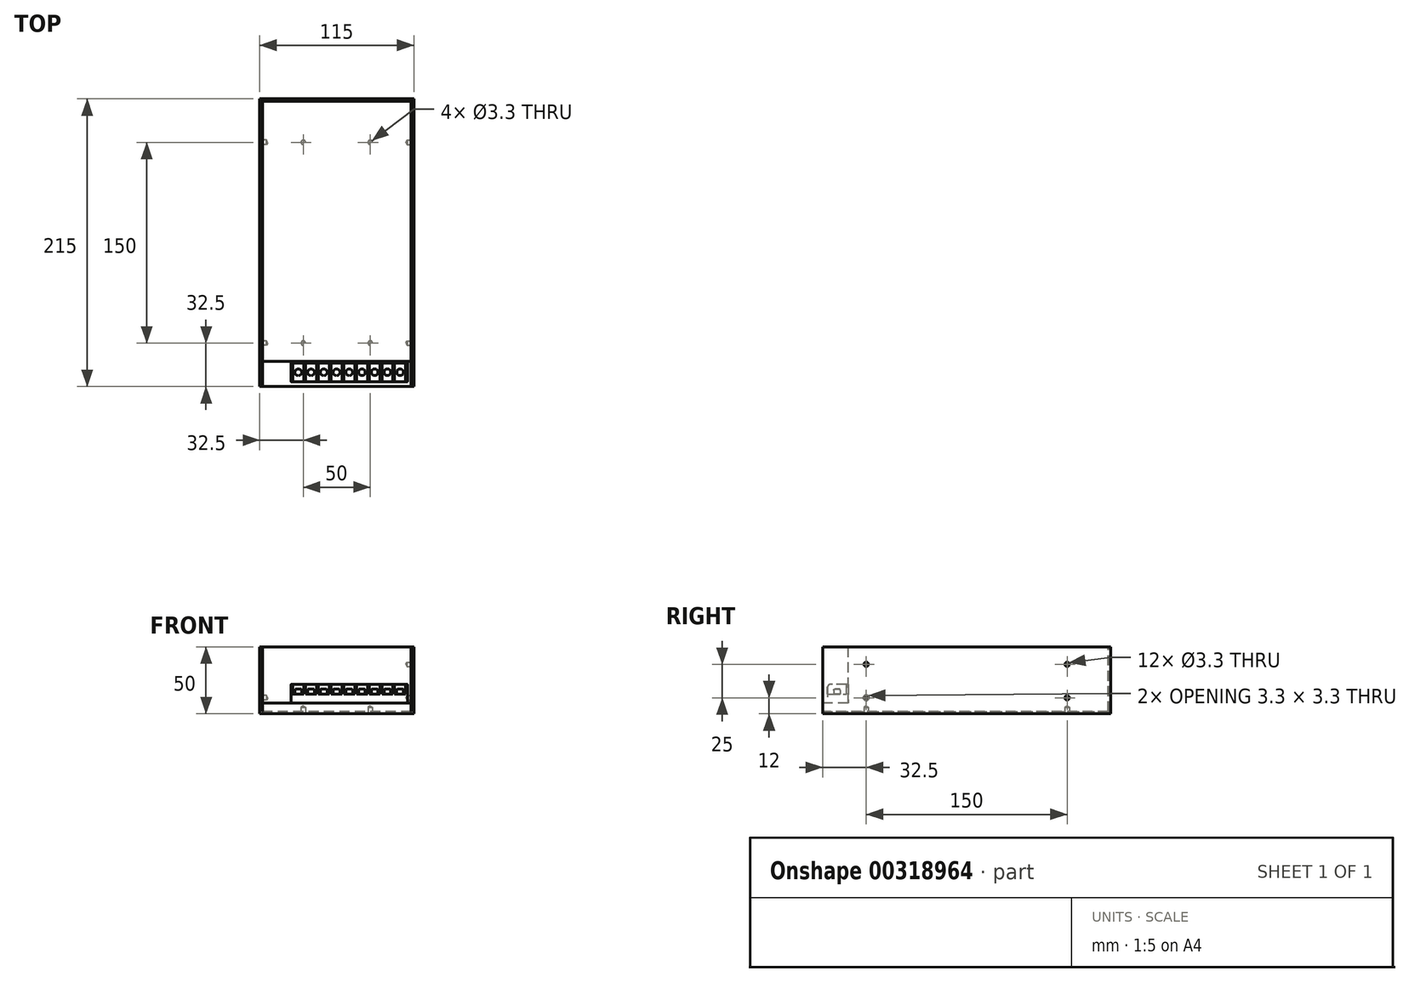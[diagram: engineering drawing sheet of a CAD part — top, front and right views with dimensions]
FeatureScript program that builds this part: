
annotation { "Feature Type Name" : "Feature", "Feature Type Description" : "" }
export const myFeature = defineFeature(function(context is Context, id is Id, definition is map)
    precondition{}
    {
        {
            var Q0;
            Q0=qCreatedBy(makeId("Front.planeOp"),FACE);
            var sketch = newSketch(context, id + "F0", { "sketchPlane" : qUnion([Q0])});
            skLineSegment(sketch, "E0.bottom", {"start": v(-57.5, 25) * mm, "end": v(0, 25) * mm});
            skLineSegment(sketch, "E0.top", {"start": v(-57.5, -25) * mm, "end": v(0, -25) * mm});
            skLineSegment(sketch, "E0.left", {"start": v(-57.5, 25) * mm, "end": v(-57.5, -25) * mm});
            skLineSegment(sketch, "E0.right", {"start": v(0, 25) * mm, "end": v(0, -25) * mm});
            skLineSegment(sketch, "E1", {"start": v(0, 0) * mm, "end": v(0, 48.13) * mm, "construction": true});
            skLineSegment(sketch, "E2", {"start": v(0, 0) * mm, "end": v(-98.9, 0) * mm, "construction": true});
            skPoint(sketch, "E2.endSnap0", {"position": v(0, 0) * mm});
            skSolve(sketch);
        }
        {
            var Q0;
            Q0=makeQuery(id+"F0.imprint","IMPRINT",FACE,{"disambiguationData":[TD([[makeQuery(id+"F0.imprint","IMPRINT",EDGE,{"derivedFrom":sQuery(id+"F0.wireOp",EDGE,"E0.bottom")}),-1.0]])]});
            extrude(context, id + "F1", {"entities" : qUnion([Q0]), "endBound" : BoundingType.SYMMETRIC, "depth" : 215 * mm});
        }
        {
            var Q0;
            Q0=makeQuery(id+"F1.opExtrude","SWEPT_FACE",FACE,{"disambiguationData":[OSD([sQuery(id+"F0.wireOp",EDGE,"E0.bottom")])]});
            var sketch = newSketch(context, id + "F2", { "sketchPlane" : qUnion([Q0])});
            skLineSegment(sketch, "E3.bottom", {"start": v(0, -107.5) * mm, "end": v(-55.8, -107.5) * mm});
            skLineSegment(sketch, "E3.top", {"start": v(0, -88.5) * mm, "end": v(-55.8, -88.5) * mm});
            skLineSegment(sketch, "E3.left", {"start": v(0, -107.5) * mm, "end": v(0, -88.5) * mm});
            skLineSegment(sketch, "E3.right", {"start": v(-55.8, -107.5) * mm, "end": v(-55.8, -88.5) * mm});
            skSolve(sketch);
        }
        {
            var Q0;
            Q0=makeQuery(id+"F2.imprint","IMPRINT",FACE,{"disambiguationData":[TD([[makeQuery(id+"F2.imprint","IMPRINT",EDGE,{"derivedFrom":sQuery(id+"F2.wireOp",EDGE,"E3.bottom")}),1.0]])]});
            extrude(context, id + "F3", {"entities" : qUnion([Q0]), "operationType" : NewBodyOperationType.REMOVE, "oppositeDirection" : true, "depth" : 42 * mm});
        }
        {
            var Q0;
            Q0=makeQuery(id+"F1.opExtrude","SWEPT_FACE",FACE,{"disambiguationData":[OSD([sQuery(id+"F0.wireOp",EDGE,"E0.bottom")])]});
            var sketch = newSketch(context, id + "F4", { "sketchPlane" : qUnion([Q0])});
            skLineSegment(sketch, "E4", {"start": v(-55.8, -107.5) * mm, "end": v(-55.8, 107.5) * mm});
            skLineSegment(sketch, "E5", {"start": v(-55.8, 107.5) * mm, "end": v(-55.5, 107.5) * mm});
            skLineSegment(sketch, "E6", {"start": v(-55.5, 107.5) * mm, "end": v(-55.5, 105.8) * mm});
            skLineSegment(sketch, "E7", {"start": v(-55.5, 105.8) * mm, "end": v(0, 105.8) * mm});
            skLineSegment(sketch, "E8", {"start": v(0, 105.8) * mm, "end": v(0, 105.5) * mm});
            skLineSegment(sketch, "E9", {"start": v(0, 105.5) * mm, "end": v(-55.5, 105.5) * mm});
            skLineSegment(sketch, "E10", {"start": v(-55.5, 105.5) * mm, "end": v(-55.5, -107.5) * mm});
            skLineSegment(sketch, "E11", {"start": v(-55.5, -107.5) * mm, "end": v(-55.8, -107.5) * mm});
            skSolve(sketch);
        }
        {
            var Q0;
            {var subQ1=sQuery(id+"F4.wireOp",EDGE,"E5");Q0=makeQuery(id+"F4.imprint","IMPRINT",FACE,{"disambiguationData":[TD([[makeQuery(id+"F4.imprint","IMPRINT",EDGE,{"derivedFrom":subQ1}),-1.0]])]});}
            var Q1;
            {var subQ0=sQuery(id+"F4.wireOp",EDGE,"E11");Q1=makeQuery(id+"F4.imprint","IMPRINT",FACE,{"disambiguationData":[TD([[makeQuery(id+"F4.imprint","IMPRINT",EDGE,{"derivedFrom":subQ0}),-1.0]])]});}
            extrude(context, id + "F5", {"entities" : qUnion([Q0, Q1]), "operationType" : NewBodyOperationType.REMOVE, "oppositeDirection" : true, "depth" : 48.3 * mm});
        }
        {
            var Q0;
            Q0=makeQuery(id+"F1.opExtrude","SWEPT_BODY",BODY,{"disambiguationData":[OSD([sQuery(id+"F0.wireOp",EDGE,"E0.bottom"),sQuery(id+"F0.wireOp",EDGE,"E0.top"),sQuery(id+"F0.wireOp",EDGE,"E0.left"),sQuery(id+"F0.wireOp",EDGE,"E0.right")])]});
            var Q1;
            Q1=qCreatedBy(makeId("Right.planeOp"),FACE);
            mirror(context, id + "F6", {"operationType" : NewBodyOperationType.ADD, "entities" : qUnion([Q0]), "mirrorPlane" : qUnion([Q1])});
        }
        {
            var Q0;
            {var subQ0=makeQuery(id+"F3.boolean.opBoolean","COPY",FACE,{"derivedFrom":makeQuery(id+"F3.opExtrude","CAP_FACE",FACE,{"disambiguationData":[OSD([sQuery(id+"F2.wireOp",EDGE,"E3.bottom"),sQuery(id+"F2.wireOp",EDGE,"E3.top"),sQuery(id+"F2.wireOp",EDGE,"E3.left"),sQuery(id+"F2.wireOp",EDGE,"E3.right")])],"isStart":false})});Q0=makeQuery(id+"F6.boolean.opBoolean","MERGE",FACE,{"derivedFrom":[subQ0,makeQuery(id+"F6.opPattern","COPY",FACE,{"derivedFrom":subQ0,"instanceName":"1"})]});}
            var sketch = newSketch(context, id + "F7", { "sketchPlane" : qUnion([Q0])});
            skLineSegment(sketch, "E12.bottom", {"start": v(-34.2, -88.5) * mm, "end": v(52.8, -88.5) * mm});
            skLineSegment(sketch, "E12.top", {"start": v(-34.2, -103.8) * mm, "end": v(52.8, -103.8) * mm});
            skLineSegment(sketch, "E12.left", {"start": v(-34.2, -88.5) * mm, "end": v(-34.2, -103.8) * mm});
            skLineSegment(sketch, "E12.right", {"start": v(52.8, -88.5) * mm, "end": v(52.8, -103.8) * mm});
            skSolve(sketch);
        }
        {
            var Q0;
            Q0=makeQuery(id+"F7.imprint","IMPRINT",FACE,{"disambiguationData":[TD([[makeQuery(id+"F7.imprint","IMPRINT",EDGE,{"derivedFrom":sQuery(id+"F7.wireOp",EDGE,"E12.bottom")}),1.0]])]});
            extrude(context, id + "F8", {"entities" : qUnion([Q0]), "depth" : 14 * mm});
        }
        {
            var Q0;
            Q0=makeQuery(id+"F8.opExtrude","CAP_FACE",FACE,{"disambiguationData":[OSD([sQuery(id+"F7.wireOp",EDGE,"E12.bottom"),sQuery(id+"F7.wireOp",EDGE,"E12.top"),sQuery(id+"F7.wireOp",EDGE,"E12.left"),sQuery(id+"F7.wireOp",EDGE,"E12.right")])],"isStart":false});
            var sketch = newSketch(context, id + "F9", { "sketchPlane" : qUnion([Q0])});
            skLineSegment(sketch, "E13", {"start": v(-32.8, -103.8) * mm, "end": v(-32.8, -89.8) * mm});
            skLineSegment(sketch, "E14", {"start": v(-32.8, -89.8) * mm, "end": v(-24.6, -89.8) * mm});
            skLineSegment(sketch, "E15", {"start": v(-24.6, -89.8) * mm, "end": v(-24.6, -103.8) * mm});
            skLineSegment(sketch, "E16", {"start": v(-24.6, -103.8) * mm, "end": v(-32.8, -103.8) * mm});
            skLineSegment(sketch, "E17.1.0.0", {"start": v(-23.3, -103.8) * mm, "end": v(-23.3, -89.8) * mm});
            skLineSegment(sketch, "E17.1.0.1", {"start": v(-15.1, -103.8) * mm, "end": v(-23.3, -103.8) * mm});
            skLineSegment(sketch, "E17.1.0.2", {"start": v(-15.1, -89.8) * mm, "end": v(-15.1, -103.8) * mm});
            skLineSegment(sketch, "E17.1.0.3", {"start": v(-23.3, -89.8) * mm, "end": v(-15.1, -89.8) * mm});
            skLineSegment(sketch, "E17.2.0.0", {"start": v(-13.8, -103.8) * mm, "end": v(-13.8, -89.8) * mm});
            skLineSegment(sketch, "E17.2.0.1", {"start": v(-5.6, -103.8) * mm, "end": v(-13.8, -103.8) * mm});
            skLineSegment(sketch, "E17.2.0.2", {"start": v(-5.6, -89.8) * mm, "end": v(-5.6, -103.8) * mm});
            skLineSegment(sketch, "E17.2.0.3", {"start": v(-13.8, -89.8) * mm, "end": v(-5.6, -89.8) * mm});
            skLineSegment(sketch, "E17.3.0.0", {"start": v(-4.3, -103.8) * mm, "end": v(-4.3, -89.8) * mm});
            skLineSegment(sketch, "E17.3.0.1", {"start": v(3.9, -103.8) * mm, "end": v(-4.3, -103.8) * mm});
            skLineSegment(sketch, "E17.3.0.2", {"start": v(3.9, -89.8) * mm, "end": v(3.9, -103.8) * mm});
            skLineSegment(sketch, "E17.3.0.3", {"start": v(-4.3, -89.8) * mm, "end": v(3.9, -89.8) * mm});
            skLineSegment(sketch, "E17.4.0.0", {"start": v(5.2, -103.8) * mm, "end": v(5.2, -89.8) * mm});
            skLineSegment(sketch, "E17.4.0.1", {"start": v(13.4, -103.8) * mm, "end": v(5.2, -103.8) * mm});
            skLineSegment(sketch, "E17.4.0.2", {"start": v(13.4, -89.8) * mm, "end": v(13.4, -103.8) * mm});
            skLineSegment(sketch, "E17.4.0.3", {"start": v(5.2, -89.8) * mm, "end": v(13.4, -89.8) * mm});
            skLineSegment(sketch, "E17.5.0.0", {"start": v(14.7, -103.8) * mm, "end": v(14.7, -89.8) * mm});
            skLineSegment(sketch, "E17.5.0.1", {"start": v(22.9, -103.8) * mm, "end": v(14.7, -103.8) * mm});
            skLineSegment(sketch, "E17.5.0.2", {"start": v(22.9, -89.8) * mm, "end": v(22.9, -103.8) * mm});
            skLineSegment(sketch, "E17.5.0.3", {"start": v(14.7, -89.8) * mm, "end": v(22.9, -89.8) * mm});
            skLineSegment(sketch, "E17.6.0.0", {"start": v(24.2, -103.8) * mm, "end": v(24.2, -89.8) * mm});
            skLineSegment(sketch, "E17.6.0.1", {"start": v(32.4, -103.8) * mm, "end": v(24.2, -103.8) * mm});
            skLineSegment(sketch, "E17.6.0.2", {"start": v(32.4, -89.8) * mm, "end": v(32.4, -103.8) * mm});
            skLineSegment(sketch, "E17.6.0.3", {"start": v(24.2, -89.8) * mm, "end": v(32.4, -89.8) * mm});
            skLineSegment(sketch, "E17.7.0.0", {"start": v(33.7, -103.8) * mm, "end": v(33.7, -89.8) * mm});
            skLineSegment(sketch, "E17.7.0.1", {"start": v(41.9, -103.8) * mm, "end": v(33.7, -103.8) * mm});
            skLineSegment(sketch, "E17.7.0.2", {"start": v(41.9, -89.8) * mm, "end": v(41.9, -103.8) * mm});
            skLineSegment(sketch, "E17.7.0.3", {"start": v(33.7, -89.8) * mm, "end": v(41.9, -89.8) * mm});
            skLineSegment(sketch, "E17.8.0.0", {"start": v(43.2, -103.8) * mm, "end": v(43.2, -89.8) * mm});
            skLineSegment(sketch, "E17.8.0.1", {"start": v(51.4, -103.8) * mm, "end": v(43.2, -103.8) * mm});
            skLineSegment(sketch, "E17.8.0.2", {"start": v(51.4, -89.8) * mm, "end": v(51.4, -103.8) * mm});
            skLineSegment(sketch, "E17.8.0.3", {"start": v(43.2, -89.8) * mm, "end": v(51.4, -89.8) * mm});
            skLineSegment(sketch, "E17.direction1", {"start": v(-32.8, -103.8) * mm, "end": v(-23.3, -103.8) * mm, "construction": true});
            skSolve(sketch);
        }
        {
            var Q0;
            Q0=makeQuery(id+"F9.imprint","IMPRINT",FACE,{"disambiguationData":[TD([[makeQuery(id+"F9.imprint","IMPRINT",EDGE,{"derivedFrom":sQuery(id+"F9.wireOp",EDGE,"E13")}),-1.0]])]});
            var Q1;
            Q1=makeQuery(id+"F9.imprint","IMPRINT",FACE,{"disambiguationData":[TD([[makeQuery(id+"F9.imprint","IMPRINT",EDGE,{"derivedFrom":sQuery(id+"F9.wireOp",EDGE,"E17.1.0.0")}),-1.0]])]});
            var Q2;
            Q2=makeQuery(id+"F9.imprint","IMPRINT",FACE,{"disambiguationData":[TD([[makeQuery(id+"F9.imprint","IMPRINT",EDGE,{"derivedFrom":sQuery(id+"F9.wireOp",EDGE,"E17.2.0.0")}),-1.0]])]});
            var Q3;
            Q3=makeQuery(id+"F9.imprint","IMPRINT",FACE,{"disambiguationData":[TD([[makeQuery(id+"F9.imprint","IMPRINT",EDGE,{"derivedFrom":sQuery(id+"F9.wireOp",EDGE,"E17.3.0.0")}),-1.0]])]});
            var Q4;
            Q4=makeQuery(id+"F9.imprint","IMPRINT",FACE,{"disambiguationData":[TD([[makeQuery(id+"F9.imprint","IMPRINT",EDGE,{"derivedFrom":sQuery(id+"F9.wireOp",EDGE,"E17.4.0.0")}),-1.0]])]});
            var Q5;
            Q5=makeQuery(id+"F9.imprint","IMPRINT",FACE,{"disambiguationData":[TD([[makeQuery(id+"F9.imprint","IMPRINT",EDGE,{"derivedFrom":sQuery(id+"F9.wireOp",EDGE,"E17.5.0.0")}),-1.0]])]});
            var Q6;
            Q6=makeQuery(id+"F9.imprint","IMPRINT",FACE,{"disambiguationData":[TD([[makeQuery(id+"F9.imprint","IMPRINT",EDGE,{"derivedFrom":sQuery(id+"F9.wireOp",EDGE,"E17.6.0.0")}),-1.0]])]});
            var Q7;
            Q7=makeQuery(id+"F9.imprint","IMPRINT",FACE,{"disambiguationData":[TD([[makeQuery(id+"F9.imprint","IMPRINT",EDGE,{"derivedFrom":sQuery(id+"F9.wireOp",EDGE,"E17.7.0.0")}),-1.0]])]});
            var Q8;
            Q8=makeQuery(id+"F9.imprint","IMPRINT",FACE,{"disambiguationData":[TD([[makeQuery(id+"F9.imprint","IMPRINT",EDGE,{"derivedFrom":sQuery(id+"F9.wireOp",EDGE,"E17.8.0.0")}),-1.0]])]});
            extrude(context, id + "F10", {"entities" : qUnion([Q0, Q1, Q2, Q3, Q4, Q5, Q6, Q7, Q8]), "operationType" : NewBodyOperationType.REMOVE, "oppositeDirection" : true, "depth" : 7.4 * mm});
        }
        {
            var Q0;
            {var subQ0=sQuery(id+"F7.wireOp",EDGE,"E12.left");var subQ1=sQuery(id+"F7.wireOp",EDGE,"E12.top");Q0=makeQuery(id+"F10.boolean.opBoolean","SPLIT",EDGE,{"disambiguationData":[TD([makeQuery(id+"F8.opExtrude","SWEPT_FACE",FACE,{"disambiguationData":[OSD([subQ0])]})])],"derivedFrom":makeQuery(id+"F8.opExtrude","CAP_EDGE",EDGE,{"disambiguationData":[OSD([subQ1])],"isStart":false})});}
            var Q1;
            {var subQ0=sQuery(id+"F7.wireOp",EDGE,"E12.top");Q1=makeQuery(id+"F10.boolean.opBoolean","SPLIT",EDGE,{"disambiguationData":[TD([makeQuery(id+"F10.opExtrude","SWEPT_FACE",FACE,{"disambiguationData":[OSD([sQuery(id+"F9.wireOp",EDGE,"E15")])]})])],"derivedFrom":makeQuery(id+"F8.opExtrude","CAP_EDGE",EDGE,{"disambiguationData":[OSD([subQ0])],"isStart":false})});}
            var Q2;
            {var subQ0=sQuery(id+"F7.wireOp",EDGE,"E12.top");Q2=makeQuery(id+"F10.boolean.opBoolean","SPLIT",EDGE,{"disambiguationData":[TD([makeQuery(id+"F10.opExtrude","SWEPT_FACE",FACE,{"disambiguationData":[OSD([sQuery(id+"F9.wireOp",EDGE,"E17.1.0.2")])]})])],"derivedFrom":makeQuery(id+"F8.opExtrude","CAP_EDGE",EDGE,{"disambiguationData":[OSD([subQ0])],"isStart":false})});}
            var Q3;
            {var subQ0=sQuery(id+"F7.wireOp",EDGE,"E12.top");Q3=makeQuery(id+"F10.boolean.opBoolean","SPLIT",EDGE,{"disambiguationData":[TD([makeQuery(id+"F10.opExtrude","SWEPT_FACE",FACE,{"disambiguationData":[OSD([sQuery(id+"F9.wireOp",EDGE,"E17.2.0.2")])]})])],"derivedFrom":makeQuery(id+"F8.opExtrude","CAP_EDGE",EDGE,{"disambiguationData":[OSD([subQ0])],"isStart":false})});}
            var Q4;
            {var subQ0=sQuery(id+"F7.wireOp",EDGE,"E12.top");Q4=makeQuery(id+"F10.boolean.opBoolean","SPLIT",EDGE,{"disambiguationData":[TD([makeQuery(id+"F10.opExtrude","SWEPT_FACE",FACE,{"disambiguationData":[OSD([sQuery(id+"F9.wireOp",EDGE,"E17.3.0.2")])]})])],"derivedFrom":makeQuery(id+"F8.opExtrude","CAP_EDGE",EDGE,{"disambiguationData":[OSD([subQ0])],"isStart":false})});}
            var Q5;
            {var subQ0=sQuery(id+"F7.wireOp",EDGE,"E12.top");Q5=makeQuery(id+"F10.boolean.opBoolean","SPLIT",EDGE,{"disambiguationData":[TD([makeQuery(id+"F10.opExtrude","SWEPT_FACE",FACE,{"disambiguationData":[OSD([sQuery(id+"F9.wireOp",EDGE,"E17.4.0.2")])]})])],"derivedFrom":makeQuery(id+"F8.opExtrude","CAP_EDGE",EDGE,{"disambiguationData":[OSD([subQ0])],"isStart":false})});}
            var Q6;
            {var subQ0=sQuery(id+"F7.wireOp",EDGE,"E12.top");Q6=makeQuery(id+"F10.boolean.opBoolean","SPLIT",EDGE,{"disambiguationData":[TD([makeQuery(id+"F10.opExtrude","SWEPT_FACE",FACE,{"disambiguationData":[OSD([sQuery(id+"F9.wireOp",EDGE,"E17.5.0.2")])]})])],"derivedFrom":makeQuery(id+"F8.opExtrude","CAP_EDGE",EDGE,{"disambiguationData":[OSD([subQ0])],"isStart":false})});}
            var Q7;
            {var subQ0=sQuery(id+"F7.wireOp",EDGE,"E12.top");Q7=makeQuery(id+"F10.boolean.opBoolean","SPLIT",EDGE,{"disambiguationData":[TD([makeQuery(id+"F10.opExtrude","SWEPT_FACE",FACE,{"disambiguationData":[OSD([sQuery(id+"F9.wireOp",EDGE,"E17.6.0.2")])]})])],"derivedFrom":makeQuery(id+"F8.opExtrude","CAP_EDGE",EDGE,{"disambiguationData":[OSD([subQ0])],"isStart":false})});}
            var Q8;
            {var subQ0=sQuery(id+"F7.wireOp",EDGE,"E12.top");Q8=makeQuery(id+"F10.boolean.opBoolean","SPLIT",EDGE,{"disambiguationData":[TD([makeQuery(id+"F10.opExtrude","SWEPT_FACE",FACE,{"disambiguationData":[OSD([sQuery(id+"F9.wireOp",EDGE,"E17.7.0.2")])]})])],"derivedFrom":makeQuery(id+"F8.opExtrude","CAP_EDGE",EDGE,{"disambiguationData":[OSD([subQ0])],"isStart":false})});}
            var Q9;
            {var subQ0=sQuery(id+"F7.wireOp",EDGE,"E12.right");var subQ1=sQuery(id+"F7.wireOp",EDGE,"E12.top");Q9=makeQuery(id+"F10.boolean.opBoolean","SPLIT",EDGE,{"disambiguationData":[TD([makeQuery(id+"F8.opExtrude","SWEPT_FACE",FACE,{"disambiguationData":[OSD([subQ0])]})])],"derivedFrom":makeQuery(id+"F8.opExtrude","CAP_EDGE",EDGE,{"disambiguationData":[OSD([subQ1])],"isStart":false})});}
            fillet(context, id + "F11", {"entities" : qUnion([Q0, Q1, Q2, Q3, Q4, Q5, Q6, Q7, Q8, Q9]), "radius" : 2 * mm, "tangentPropagation" : true, "allowEdgeOverflow" : false});
        }
        {
            var Q0;
            Q0=makeQuery(id+"F10.boolean.opBoolean","COPY",FACE,{"derivedFrom":makeQuery(id+"F10.opExtrude","CAP_FACE",FACE,{"disambiguationData":[OSD([sQuery(id+"F9.wireOp",EDGE,"E13"),sQuery(id+"F9.wireOp",EDGE,"E14"),sQuery(id+"F9.wireOp",EDGE,"E15"),sQuery(id+"F9.wireOp",EDGE,"E16")])],"isStart":false})});
            var sketch = newSketch(context, id + "F12", { "sketchPlane" : qUnion([Q0])});
            skLineSegment(sketch, "E18", {"start": v(-32.8, -89.8) * mm, "end": v(-24.6, -103.8) * mm, "construction": true});
            skCircle(sketch, "E19", {"center": v(-28.7, -96.8) * mm, "radius": 2.5 * mm});
            skCircle(sketch, "E20.1.0.0", {"center": v(-19.2, -96.8) * mm, "radius": 2.5 * mm});
            skCircle(sketch, "E20.2.0.0", {"center": v(-9.7, -96.8) * mm, "radius": 2.5 * mm});
            skCircle(sketch, "E20.3.0.0", {"center": v(-0.2, -96.8) * mm, "radius": 2.5 * mm});
            skCircle(sketch, "E20.4.0.0", {"center": v(9.3, -96.8) * mm, "radius": 2.5 * mm});
            skCircle(sketch, "E20.5.0.0", {"center": v(18.8, -96.8) * mm, "radius": 2.5 * mm});
            skCircle(sketch, "E20.6.0.0", {"center": v(28.3, -96.8) * mm, "radius": 2.5 * mm});
            skCircle(sketch, "E20.7.0.0", {"center": v(37.8, -96.8) * mm, "radius": 2.5 * mm});
            skCircle(sketch, "E20.8.0.0", {"center": v(47.3, -96.8) * mm, "radius": 2.5 * mm});
            skLineSegment(sketch, "E20.direction1", {"start": v(-28.7, -96.8) * mm, "end": v(-19.2, -96.8) * mm, "construction": true});
            skSolve(sketch);
        }
        {
            var Q0;
            Q0=makeQuery(id+"F12.imprint","IMPRINT",FACE,{"disambiguationData":[TD([[makeQuery(id+"F12.imprint","IMPRINT",EDGE,{"derivedFrom":sQuery(id+"F12.wireOp",EDGE,"E19")}),1.0]])]});
            var Q1;
            Q1=makeQuery(id+"F12.imprint","IMPRINT",FACE,{"disambiguationData":[TD([[makeQuery(id+"F12.imprint","IMPRINT",EDGE,{"derivedFrom":sQuery(id+"F12.wireOp",EDGE,"E20.1.0.0")}),1.0]])]});
            var Q2;
            Q2=makeQuery(id+"F12.imprint","IMPRINT",FACE,{"disambiguationData":[TD([[makeQuery(id+"F12.imprint","IMPRINT",EDGE,{"derivedFrom":sQuery(id+"F12.wireOp",EDGE,"E20.2.0.0")}),1.0]])]});
            var Q3;
            Q3=makeQuery(id+"F12.imprint","IMPRINT",FACE,{"disambiguationData":[TD([[makeQuery(id+"F12.imprint","IMPRINT",EDGE,{"derivedFrom":sQuery(id+"F12.wireOp",EDGE,"E20.3.0.0")}),1.0]])]});
            var Q4;
            Q4=makeQuery(id+"F12.imprint","IMPRINT",FACE,{"disambiguationData":[TD([[makeQuery(id+"F12.imprint","IMPRINT",EDGE,{"derivedFrom":sQuery(id+"F12.wireOp",EDGE,"E20.4.0.0")}),1.0]])]});
            var Q5;
            Q5=makeQuery(id+"F12.imprint","IMPRINT",FACE,{"disambiguationData":[TD([[makeQuery(id+"F12.imprint","IMPRINT",EDGE,{"derivedFrom":sQuery(id+"F12.wireOp",EDGE,"E20.5.0.0")}),1.0]])]});
            var Q6;
            Q6=makeQuery(id+"F12.imprint","IMPRINT",FACE,{"disambiguationData":[TD([[makeQuery(id+"F12.imprint","IMPRINT",EDGE,{"derivedFrom":sQuery(id+"F12.wireOp",EDGE,"E20.6.0.0")}),1.0]])]});
            var Q7;
            Q7=makeQuery(id+"F12.imprint","IMPRINT",FACE,{"disambiguationData":[TD([[makeQuery(id+"F12.imprint","IMPRINT",EDGE,{"derivedFrom":sQuery(id+"F12.wireOp",EDGE,"E20.7.0.0")}),1.0]])]});
            var Q8;
            Q8=makeQuery(id+"F12.imprint","IMPRINT",FACE,{"disambiguationData":[TD([[makeQuery(id+"F12.imprint","IMPRINT",EDGE,{"derivedFrom":sQuery(id+"F12.wireOp",EDGE,"E20.8.0.0")}),1.0]])]});
            var Q9;
            Q9=sQuery(id+"F12.wireOp",EDGE,"E19");
            extrude(context, id + "F13", {"entities" : qUnion([Q0, Q1, Q2, Q3, Q4, Q5, Q6, Q7, Q8]), "operationType" : NewBodyOperationType.ADD, "surfaceEntities" : qUnion([Q9]), "depth" : 4 * mm});
        }
        {
            var Q0;
            Q0=makeQuery(id+"F13.opExtrude","CAP_EDGE",EDGE,{"disambiguationData":[OSD([sQuery(id+"F12.wireOp",EDGE,"E19")])],"isStart":false});
            var Q1;
            Q1=makeQuery(id+"F13.opExtrude","CAP_EDGE",EDGE,{"disambiguationData":[OSD([sQuery(id+"F12.wireOp",EDGE,"E20.1.0.0")])],"isStart":false});
            var Q2;
            Q2=makeQuery(id+"F13.opExtrude","CAP_EDGE",EDGE,{"disambiguationData":[OSD([sQuery(id+"F12.wireOp",EDGE,"E20.2.0.0")])],"isStart":false});
            var Q3;
            Q3=makeQuery(id+"F13.opExtrude","CAP_EDGE",EDGE,{"disambiguationData":[OSD([sQuery(id+"F12.wireOp",EDGE,"E20.3.0.0")])],"isStart":false});
            var Q4;
            Q4=makeQuery(id+"F13.opExtrude","CAP_EDGE",EDGE,{"disambiguationData":[OSD([sQuery(id+"F12.wireOp",EDGE,"E20.4.0.0")])],"isStart":false});
            var Q5;
            Q5=makeQuery(id+"F13.opExtrude","CAP_EDGE",EDGE,{"disambiguationData":[OSD([sQuery(id+"F12.wireOp",EDGE,"E20.5.0.0")])],"isStart":false});
            var Q6;
            Q6=makeQuery(id+"F13.opExtrude","CAP_EDGE",EDGE,{"disambiguationData":[OSD([sQuery(id+"F12.wireOp",EDGE,"E20.6.0.0")])],"isStart":false});
            var Q7;
            Q7=makeQuery(id+"F13.opExtrude","CAP_EDGE",EDGE,{"disambiguationData":[OSD([sQuery(id+"F12.wireOp",EDGE,"E20.7.0.0")])],"isStart":false});
            var Q8;
            Q8=makeQuery(id+"F13.opExtrude","CAP_EDGE",EDGE,{"disambiguationData":[OSD([sQuery(id+"F12.wireOp",EDGE,"E20.8.0.0")])],"isStart":false});
            fillet(context, id + "F14", {"entities" : qUnion([Q0, Q1, Q2, Q3, Q4, Q5, Q6, Q7, Q8]), "radius" : 1 * mm, "tangentPropagation" : true, "allowEdgeOverflow" : false});
        }
        {
            var Q0;
            Q0=makeQuery(id+"F1.opExtrude","SWEPT_FACE",FACE,{"disambiguationData":[OSD([sQuery(id+"F0.wireOp",EDGE,"E0.left")])]});
            var sketch = newSketch(context, id + "F15", { "sketchPlane" : qUnion([Q0])});
            skLineSegment(sketch, "E21", {"start": v(-75, -13) * mm, "end": v(75, -13) * mm});
            skLineSegment(sketch, "E22", {"start": v(0, 0) * mm, "end": v(0, -13) * mm});
            skSolve(sketch);
        }
        {
            var Q0;
            Q0=makeQuery(id+"F6.opPattern","COPY",FACE,{"derivedFrom":makeQuery(id+"F1.opExtrude","SWEPT_FACE",FACE,{"disambiguationData":[OSD([sQuery(id+"F0.wireOp",EDGE,"E0.left")])]}),"instanceName":"1"});
            var sketch = newSketch(context, id + "F16", { "sketchPlane" : qUnion([Q0])});
            skPoint(sketch, "E23.0", {"position": v(-75, -13) * mm});
            skPoint(sketch, "E23.1", {"position": v(75, -13) * mm});
            skPoint(sketch, "E24", {"position": v(-75, 12) * mm});
            skPoint(sketch, "E25", {"position": v(75, 12) * mm});
            skSolve(sketch);
        }
        {
            var Q0;
            {var subQ0=makeQuery(id+"F1.opExtrude","SWEPT_FACE",FACE,{"disambiguationData":[OSD([sQuery(id+"F0.wireOp",EDGE,"E0.top")])]});Q0=makeQuery(id+"F6.boolean.opBoolean","MERGE",FACE,{"derivedFrom":[subQ0,makeQuery(id+"F6.opPattern","COPY",FACE,{"derivedFrom":subQ0,"instanceName":"1"})]});}
            var sketch = newSketch(context, id + "F17", { "sketchPlane" : qUnion([Q0])});
            skLineSegment(sketch, "E26", {"start": v(-21.97, 0) * mm, "end": v(0, 0) * mm, "construction": true});
            skLineSegment(sketch, "E27", {"start": v(0, 0) * mm, "end": v(0, 32.91) * mm, "construction": true});
            skPoint(sketch, "E28", {"position": v(-25, 75) * mm});
            skPoint(sketch, "E29.MirrorP", {"position": v(-25, -75) * mm});
            skPoint(sketch, "E30.MirrorP", {"position": v(25, -75) * mm});
            skPoint(sketch, "E31.MirrorP", {"position": v(25, 75) * mm});
            skSolve(sketch);
        }
        {
            var Q0;
            Q0=sQuery(id+"F15.wireOp",VERTEX,"E21.start");
            var Q1;
            Q1=sQuery(id+"F15.wireOp",VERTEX,"E21.end");
            var Q2;
            Q2=sQuery(id+"F17.wireOp",VERTEX,"E29.MirrorP");
            var Q3;
            Q3=sQuery(id+"F17.wireOp",VERTEX,"E28");
            var Q4;
            Q4=sQuery(id+"F17.wireOp",VERTEX,"E30.MirrorP");
            var Q5;
            Q5=sQuery(id+"F17.wireOp",VERTEX,"E31.MirrorP");
            var Q6;
            Q6=sQuery(id+"F16.wireOp",VERTEX,"E23.0");
            var Q7;
            Q7=sQuery(id+"F16.wireOp",VERTEX,"E24");
            var Q8;
            Q8=sQuery(id+"F16.wireOp",VERTEX,"E25");
            var Q9;
            Q9=sQuery(id+"F16.wireOp",VERTEX,"E23.1");
            var Q10;
            Q10=makeQuery(id+"F1.opExtrude","SWEPT_BODY",BODY,{"disambiguationData":[OSD([sQuery(id+"F0.wireOp",EDGE,"E0.bottom"),sQuery(id+"F0.wireOp",EDGE,"E0.top"),sQuery(id+"F0.wireOp",EDGE,"E0.left"),sQuery(id+"F0.wireOp",EDGE,"E0.right")])]});
            hole(context, id + "F18", {"style" : HoleStyle.SIMPLE, "endStyle" : HoleEndStyle.BLIND, "holeDiameter" : 3.3 * mm, "holeDepth" : 5 * mm, "locations" : qUnion([Q0, Q1, Q2, Q3, Q4, Q5, Q6, Q7, Q8, Q9]), "scope" : qUnion([Q10])});
        }
    });
